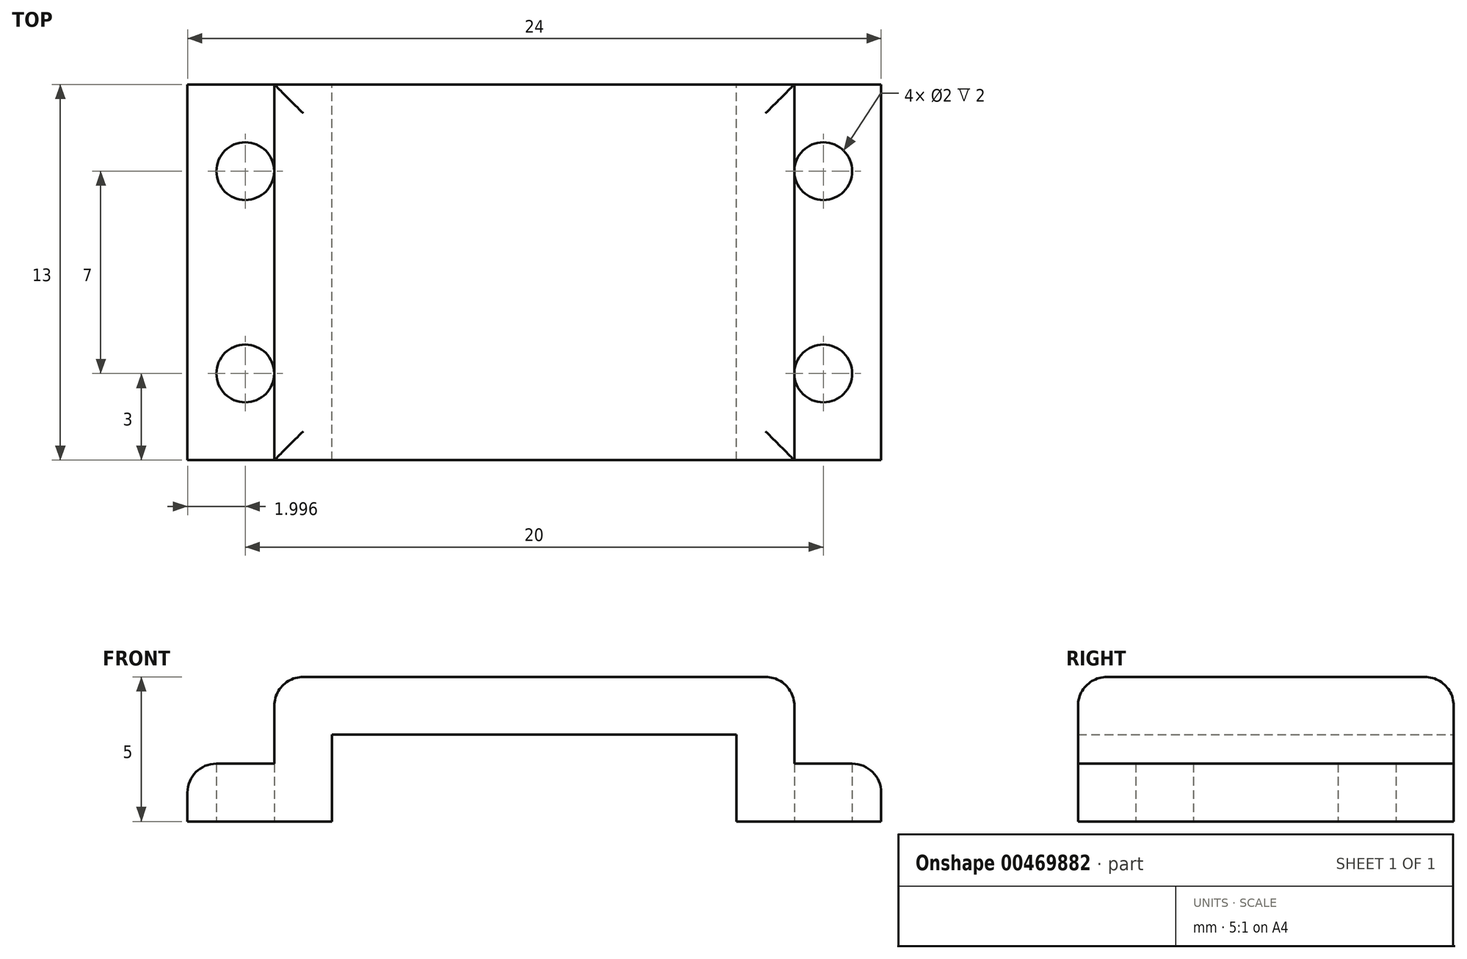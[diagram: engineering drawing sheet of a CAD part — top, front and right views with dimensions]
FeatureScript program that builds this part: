
annotation { "Feature Type Name" : "Feature", "Feature Type Description" : "" }
export const myFeature = defineFeature(function(context is Context, id is Id, definition is map)
    precondition{}
    {
        {
            var Q0;
            Q0=qCreatedBy(makeId("Front.planeOp"),FACE);
            var sketch = newSketch(context, id + "F0", { "sketchPlane" : qUnion([Q0])});
            skLineSegment(sketch, "E0", {"start": v(-18.61, 0) * mm, "end": v(-15.42, 0) * mm});
            skLineSegment(sketch, "E1", {"start": v(-15.42, 0) * mm, "end": v(-15.42, 3) * mm});
            skLineSegment(sketch, "E2", {"start": v(-15.42, 3) * mm, "end": v(-1.42, 3) * mm});
            skLineSegment(sketch, "E3", {"start": v(-1.42, 3) * mm, "end": v(-1.42, 0) * mm});
            skLineSegment(sketch, "E4", {"start": v(-1.42, 0) * mm, "end": v(3.58, 0) * mm});
            skLineSegment(sketch, "E5", {"start": v(3.58, 0) * mm, "end": v(3.58, 2) * mm});
            skLineSegment(sketch, "E6", {"start": v(3.58, 2) * mm, "end": v(0.58, 2) * mm});
            skLineSegment(sketch, "E7", {"start": v(0.58, 5) * mm, "end": v(-17.42, 5) * mm});
            skLineSegment(sketch, "E8", {"start": v(-17.42, 2) * mm, "end": v(-20.42, 2) * mm});
            skLineSegment(sketch, "E9", {"start": v(-20.42, 2) * mm, "end": v(-20.42, 0) * mm});
            skLineSegment(sketch, "E10", {"start": v(-20.42, 0) * mm, "end": v(-18.61, 0) * mm});
            skPoint(sketch, "E11.visualSharp", {"position": v(0.58, 5) * mm});
            skLineSegment(sketch, "E12", {"start": v(-17.42, 2) * mm, "end": v(-17.42, 5) * mm});
            skLineSegment(sketch, "E13", {"start": v(0.58, 2) * mm, "end": v(0.58, 5) * mm});
            skSolve(sketch);
        }
        {
            var Q0;
            Q0=makeQuery(id+"F0.imprint","IMPRINT",FACE,{"disambiguationData":[TD([[makeQuery(id+"F0.imprint","IMPRINT",EDGE,{"derivedFrom":sQuery(id+"F0.wireOp",EDGE,"E0")}),1.0]])]});
            extrude(context, id + "F1", {"entities" : qUnion([Q0]), "depth" : 13 * mm});
        }
        {
            var Q0;
            Q0=makeQuery(id+"F1.opExtrude","SWEPT_EDGE",EDGE,{"disambiguationData":[OSD([sQuery(id+"F0.wireOp",EDGE,"uJ7Fj812-s6nb-crp3-mzeZ-AZzYXzThiyhB"),sQuery(id+"F0.wireOp",EDGE,"E7")])]});
            var Q1;
            Q1=makeQuery(id+"F1.opExtrude","CAP_EDGE",EDGE,{"disambiguationData":[OSD([sQuery(id+"F0.wireOp",EDGE,"E7")])],"isStart":true});
            var Q2;
            Q2=makeQuery(id+"F1.opExtrude","SWEPT_EDGE",EDGE,{"disambiguationData":[OSD([sQuery(id+"F0.wireOp",EDGE,"E7"),sQuery(id+"F0.wireOp",EDGE,"NQvLR3vh-Jl46-lhvZ-defx-JKZYzrXmkqKB")])]});
            var Q3;
            Q3=makeQuery(id+"F1.opExtrude","SWEPT_FACE",FACE,{"disambiguationData":[OSD([sQuery(id+"F0.wireOp",EDGE,"E7")])]});
            var Q4;
            Q4=makeQuery(id+"F1.opExtrude","SWEPT_EDGE",EDGE,{"disambiguationData":[OSD([sQuery(id+"F0.wireOp",EDGE,"E5"),sQuery(id+"F0.wireOp",EDGE,"E6")])]});
            var Q5;
            Q5=makeQuery(id+"F1.opExtrude","SWEPT_EDGE",EDGE,{"disambiguationData":[OSD([sQuery(id+"F0.wireOp",EDGE,"E8"),sQuery(id+"F0.wireOp",EDGE,"E9")])]});
            fillet(context, id + "F2", {"entities" : qUnion([Q0, Q1, Q2, Q3, Q4, Q5]), "radius" : 1 * mm, "tangentPropagation" : true, "allowEdgeOverflow" : false});
        }
        {
            var Q0;
            Q0=makeQuery(id+"F1.opExtrude","SWEPT_FACE",FACE,{"disambiguationData":[OSD([sQuery(id+"F0.wireOp",EDGE,"E0"),sQuery(id+"F0.wireOp",EDGE,"E10")])]});
            var sketch = newSketch(context, id + "F3", { "sketchPlane" : qUnion([Q0])});
            skCircle(sketch, "E14", {"center": v(-18.42, 10) * mm, "radius": 1 * mm});
            skCircle(sketch, "E15", {"center": v(-18.42, 3) * mm, "radius": 1 * mm});
            skSolve(sketch);
        }
        {
            var Q0;
            Q0=makeQuery(id+"F3.imprint","IMPRINT",FACE,{"disambiguationData":[TD([[makeQuery(id+"F3.imprint","IMPRINT",EDGE,{"derivedFrom":sQuery(id+"F3.wireOp",EDGE,"E14")}),1.0]])]});
            var Q1;
            Q1=makeQuery(id+"F3.imprint","IMPRINT",FACE,{"disambiguationData":[TD([[makeQuery(id+"F3.imprint","IMPRINT",EDGE,{"derivedFrom":sQuery(id+"F3.wireOp",EDGE,"E15")}),1.0]])]});
            extrude(context, id + "F4", {"entities" : qUnion([Q0, Q1]), "operationType" : NewBodyOperationType.REMOVE, "oppositeDirection" : true, "depth" : 25 * mm});
        }
        {
            var Q0;
            Q0=makeQuery(id+"F1.opExtrude","SWEPT_FACE",FACE,{"disambiguationData":[OSD([sQuery(id+"F0.wireOp",EDGE,"E4")])]});
            var sketch = newSketch(context, id + "F5", { "sketchPlane" : qUnion([Q0])});
            skCircle(sketch, "E16", {"center": v(1.58, 10) * mm, "radius": 1 * mm});
            skCircle(sketch, "E17", {"center": v(1.58, 3) * mm, "radius": 1 * mm});
            skSolve(sketch);
        }
        {
            var Q0;
            Q0=makeQuery(id+"F5.imprint","IMPRINT",FACE,{"disambiguationData":[TD([[makeQuery(id+"F5.imprint","IMPRINT",EDGE,{"derivedFrom":sQuery(id+"F5.wireOp",EDGE,"E16")}),1.0]])]});
            var Q1;
            Q1=makeQuery(id+"F5.imprint","IMPRINT",FACE,{"disambiguationData":[TD([[makeQuery(id+"F5.imprint","IMPRINT",EDGE,{"derivedFrom":sQuery(id+"F5.wireOp",EDGE,"E17")}),1.0]])]});
            extrude(context, id + "F6", {"entities" : qUnion([Q0, Q1]), "operationType" : NewBodyOperationType.REMOVE, "oppositeDirection" : true, "depth" : 25 * mm});
        }
    });
